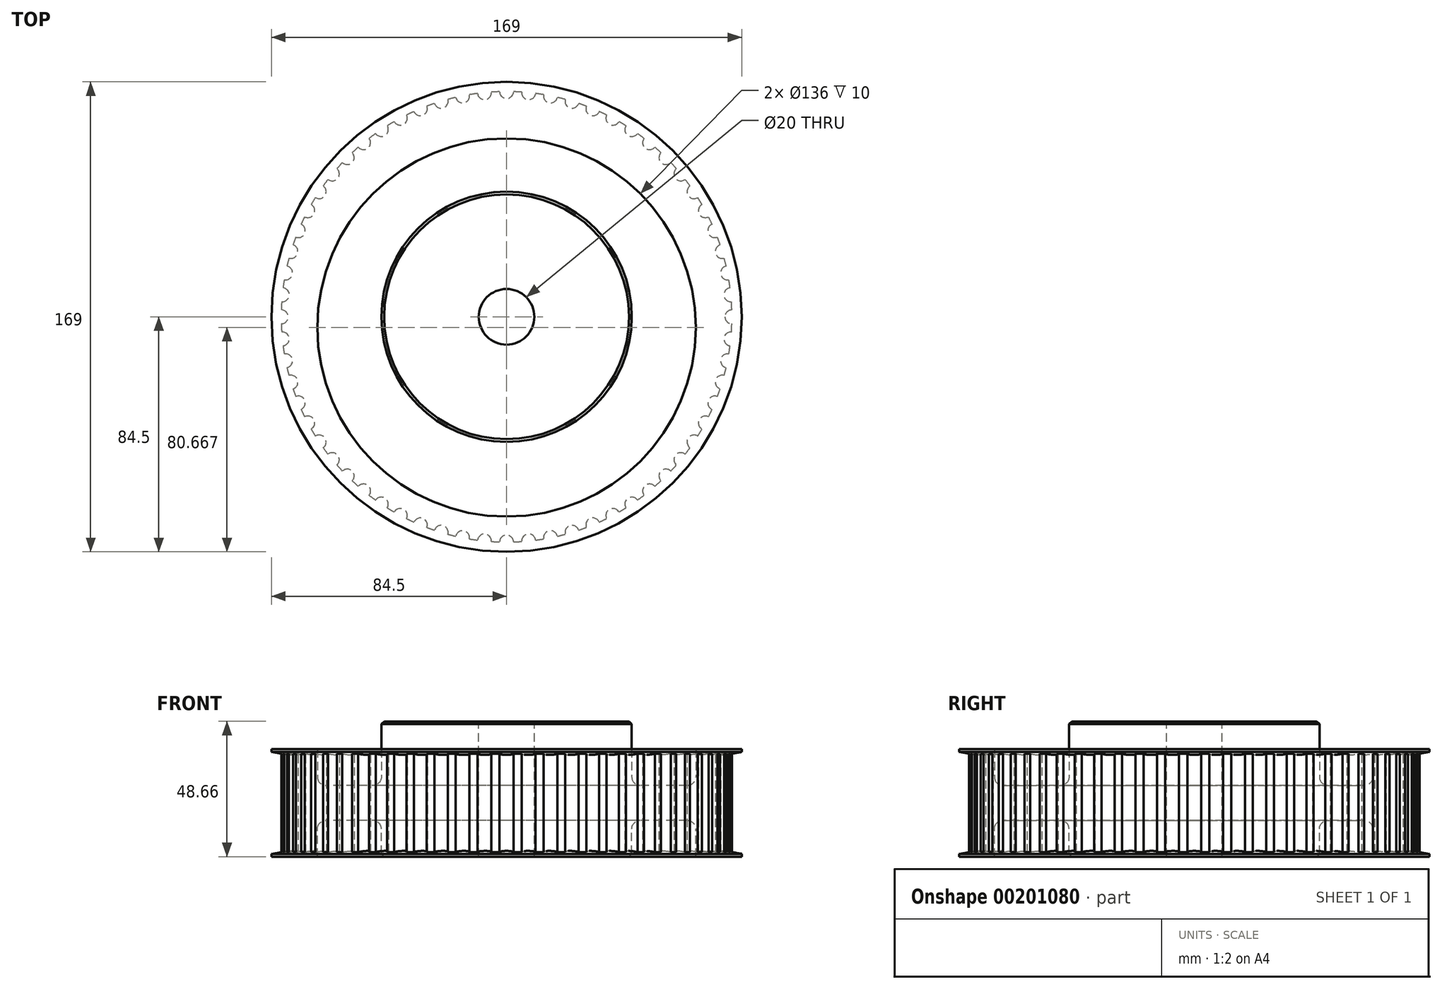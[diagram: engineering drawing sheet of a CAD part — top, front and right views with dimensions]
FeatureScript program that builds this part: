
annotation { "Feature Type Name" : "Feature", "Feature Type Description" : "" }
export const myFeature = defineFeature(function(context is Context, id is Id, definition is map)
    precondition{}
    {
        {
            var Q0;
            Q0=qCreatedBy(makeId("Top.planeOp"),FACE);
            var sketch = newSketch(context, id + "F0", { "sketchPlane" : qUnion([Q0])});
            skCircle(sketch, "E0", {"center": v(0, 0) * mm, "radius": 81 * mm});
            skCircle(sketch, "E1", {"center": v(0, 81) * mm, "radius": 2.5 * mm});
            skCircle(sketch, "E2.1.0", {"center": v(-7.94, 80.6) * mm, "radius": 2.5 * mm});
            skCircle(sketch, "E2.2.0", {"center": v(-15.8, 79.44) * mm, "radius": 2.5 * mm});
            skCircle(sketch, "E3.1.3.0", {"center": v(-23.51, 77.51) * mm, "radius": 2.5 * mm});
            skCircle(sketch, "E3.1.4.0", {"center": v(-31, 74.83) * mm, "radius": 2.5 * mm});
            skCircle(sketch, "E3.1.5.0", {"center": v(-38.18, 71.44) * mm, "radius": 2.5 * mm});
            skCircle(sketch, "E3.1.6.0", {"center": v(-45, 67.35) * mm, "radius": 2.5 * mm});
            skCircle(sketch, "E3.1.7.0", {"center": v(-51.39, 62.61) * mm, "radius": 2.5 * mm});
            skCircle(sketch, "E3.1.8.0", {"center": v(-57.28, 57.28) * mm, "radius": 2.5 * mm});
            skCircle(sketch, "E3.1.9.0", {"center": v(-62.61, 51.39) * mm, "radius": 2.5 * mm});
            skCircle(sketch, "E4.1.10.0", {"center": v(-67.35, 45) * mm, "radius": 2.5 * mm});
            skCircle(sketch, "E4.1.11.0", {"center": v(-71.44, 38.18) * mm, "radius": 2.5 * mm});
            skCircle(sketch, "E4.1.12.0", {"center": v(-74.83, 31) * mm, "radius": 2.5 * mm});
            skCircle(sketch, "E4.1.13.0", {"center": v(-77.51, 23.51) * mm, "radius": 2.5 * mm});
            skCircle(sketch, "E4.1.14.0", {"center": v(-79.44, 15.8) * mm, "radius": 2.5 * mm});
            skCircle(sketch, "E4.1.15.0", {"center": v(-80.6, 7.94) * mm, "radius": 2.5 * mm});
            skCircle(sketch, "E4.1.16.0", {"center": v(-81, 0) * mm, "radius": 2.5 * mm});
            skCircle(sketch, "E4.1.17.0", {"center": v(-80.6, -7.94) * mm, "radius": 2.5 * mm});
            skCircle(sketch, "E4.1.18.0", {"center": v(-79.44, -15.8) * mm, "radius": 2.5 * mm});
            skCircle(sketch, "E4.1.19.0", {"center": v(-77.51, -23.51) * mm, "radius": 2.5 * mm});
            skCircle(sketch, "E4.1.20.0", {"center": v(-74.83, -31) * mm, "radius": 2.5 * mm});
            skCircle(sketch, "E4.1.21.0", {"center": v(-71.44, -38.18) * mm, "radius": 2.5 * mm});
            skCircle(sketch, "E4.1.22.0", {"center": v(-67.35, -45) * mm, "radius": 2.5 * mm});
            skCircle(sketch, "E4.1.23.0", {"center": v(-62.61, -51.39) * mm, "radius": 2.5 * mm});
            skCircle(sketch, "E4.1.24.0", {"center": v(-57.28, -57.28) * mm, "radius": 2.5 * mm});
            skCircle(sketch, "E4.1.25.0", {"center": v(-51.39, -62.61) * mm, "radius": 2.5 * mm});
            skCircle(sketch, "E4.1.26.0", {"center": v(-45, -67.35) * mm, "radius": 2.5 * mm});
            skCircle(sketch, "E4.1.27.0", {"center": v(-38.18, -71.44) * mm, "radius": 2.5 * mm});
            skCircle(sketch, "E4.1.28.0", {"center": v(-31, -74.83) * mm, "radius": 2.5 * mm});
            skCircle(sketch, "E4.1.29.0", {"center": v(-23.51, -77.51) * mm, "radius": 2.5 * mm});
            skCircle(sketch, "E4.1.30.0", {"center": v(-15.8, -79.44) * mm, "radius": 2.5 * mm});
            skCircle(sketch, "E4.1.31.0", {"center": v(-7.94, -80.6) * mm, "radius": 2.5 * mm});
            skCircle(sketch, "E4.1.32.0", {"center": v(0, -81) * mm, "radius": 2.5 * mm});
            skCircle(sketch, "E4.1.33.0", {"center": v(7.94, -80.6) * mm, "radius": 2.5 * mm});
            skCircle(sketch, "E4.1.34.0", {"center": v(15.8, -79.44) * mm, "radius": 2.5 * mm});
            skCircle(sketch, "E4.1.35.0", {"center": v(23.51, -77.51) * mm, "radius": 2.5 * mm});
            skCircle(sketch, "E4.1.36.0", {"center": v(31, -74.83) * mm, "radius": 2.5 * mm});
            skCircle(sketch, "E4.1.37.0", {"center": v(38.18, -71.44) * mm, "radius": 2.5 * mm});
            skCircle(sketch, "E4.1.38.0", {"center": v(45, -67.35) * mm, "radius": 2.5 * mm});
            skCircle(sketch, "E4.1.39.0", {"center": v(51.39, -62.61) * mm, "radius": 2.5 * mm});
            skCircle(sketch, "E4.1.40.0", {"center": v(57.28, -57.28) * mm, "radius": 2.5 * mm});
            skCircle(sketch, "E4.1.41.0", {"center": v(62.61, -51.39) * mm, "radius": 2.5 * mm});
            skCircle(sketch, "E4.1.42.0", {"center": v(67.35, -45) * mm, "radius": 2.5 * mm});
            skCircle(sketch, "E4.1.43.0", {"center": v(71.44, -38.18) * mm, "radius": 2.5 * mm});
            skCircle(sketch, "E4.1.44.0", {"center": v(74.83, -31) * mm, "radius": 2.5 * mm});
            skCircle(sketch, "E4.1.45.0", {"center": v(77.51, -23.51) * mm, "radius": 2.5 * mm});
            skCircle(sketch, "E4.1.46.0", {"center": v(79.44, -15.8) * mm, "radius": 2.5 * mm});
            skCircle(sketch, "E4.1.47.0", {"center": v(80.6, -7.94) * mm, "radius": 2.5 * mm});
            skCircle(sketch, "E4.1.48.0", {"center": v(81, 0) * mm, "radius": 2.5 * mm});
            skCircle(sketch, "E4.1.49.0", {"center": v(80.6, 7.94) * mm, "radius": 2.5 * mm});
            skCircle(sketch, "E4.1.50.0", {"center": v(79.44, 15.8) * mm, "radius": 2.5 * mm});
            skCircle(sketch, "E4.1.51.0", {"center": v(77.51, 23.51) * mm, "radius": 2.5 * mm});
            skCircle(sketch, "E4.1.52.0", {"center": v(74.83, 31) * mm, "radius": 2.5 * mm});
            skCircle(sketch, "E4.1.53.0", {"center": v(71.44, 38.18) * mm, "radius": 2.5 * mm});
            skCircle(sketch, "E4.1.54.0", {"center": v(67.35, 45) * mm, "radius": 2.5 * mm});
            skCircle(sketch, "E4.1.55.0", {"center": v(62.61, 51.39) * mm, "radius": 2.5 * mm});
            skCircle(sketch, "E4.1.56.0", {"center": v(57.28, 57.28) * mm, "radius": 2.5 * mm});
            skCircle(sketch, "E4.1.57.0", {"center": v(51.39, 62.61) * mm, "radius": 2.5 * mm});
            skCircle(sketch, "E4.1.58.0", {"center": v(45, 67.35) * mm, "radius": 2.5 * mm});
            skCircle(sketch, "E4.1.59.0", {"center": v(38.18, 71.44) * mm, "radius": 2.5 * mm});
            skCircle(sketch, "E4.1.60.0", {"center": v(31, 74.83) * mm, "radius": 2.5 * mm});
            skCircle(sketch, "E4.1.61.0", {"center": v(23.51, 77.51) * mm, "radius": 2.5 * mm});
            skCircle(sketch, "E4.1.62.0", {"center": v(15.8, 79.44) * mm, "radius": 2.5 * mm});
            skCircle(sketch, "E4.1.63.0", {"center": v(7.94, 80.6) * mm, "radius": 2.5 * mm});
            skSolve(sketch);
        }
        {
            var Q0;
            Q0=makeQuery(id+"F0.imprint","IMPRINT",FACE,{"disambiguationData":[TD([[makeQuery(id+"F0.imprint","IMPRINT",EDGE,{"derivedFrom":sQuery(id+"F0.wireOp",EDGE,"E0")}),1.0]])]});
            extrude(context, id + "F1", {"entities" : qUnion([Q0]), "depth" : (32.65 / 2) * mm});
        }
        {
            var Q0;
            Q0=makeQuery(id+"F1.opExtrude","CAP_FACE",FACE,{"disambiguationData":[OSD([sQuery(id+"F0.wireOp",EDGE,"E0"),sQuery(id+"F0.wireOp",EDGE,"E1"),sQuery(id+"F0.wireOp",EDGE,"E2.1.0"),sQuery(id+"F0.wireOp",EDGE,"E2.2.0"),sQuery(id+"F0.wireOp",EDGE,"E3.1.3.0"),sQuery(id+"F0.wireOp",EDGE,"E3.1.4.0"),sQuery(id+"F0.wireOp",EDGE,"E3.1.5.0"),sQuery(id+"F0.wireOp",EDGE,"E3.1.6.0"),sQuery(id+"F0.wireOp",EDGE,"E3.1.7.0"),sQuery(id+"F0.wireOp",EDGE,"E3.1.8.0"),sQuery(id+"F0.wireOp",EDGE,"E3.1.9.0"),sQuery(id+"F0.wireOp",EDGE,"E4.1.10.0"),sQuery(id+"F0.wireOp",EDGE,"E4.1.11.0"),sQuery(id+"F0.wireOp",EDGE,"E4.1.12.0"),sQuery(id+"F0.wireOp",EDGE,"E4.1.13.0"),sQuery(id+"F0.wireOp",EDGE,"E4.1.14.0"),sQuery(id+"F0.wireOp",EDGE,"E4.1.15.0"),sQuery(id+"F0.wireOp",EDGE,"E4.1.16.0"),sQuery(id+"F0.wireOp",EDGE,"E4.1.17.0"),sQuery(id+"F0.wireOp",EDGE,"E4.1.18.0"),sQuery(id+"F0.wireOp",EDGE,"E4.1.19.0"),sQuery(id+"F0.wireOp",EDGE,"E4.1.20.0"),sQuery(id+"F0.wireOp",EDGE,"E4.1.21.0"),sQuery(id+"F0.wireOp",EDGE,"E4.1.22.0"),sQuery(id+"F0.wireOp",EDGE,"E4.1.23.0"),sQuery(id+"F0.wireOp",EDGE,"E4.1.24.0"),sQuery(id+"F0.wireOp",EDGE,"E4.1.25.0"),sQuery(id+"F0.wireOp",EDGE,"E4.1.26.0"),sQuery(id+"F0.wireOp",EDGE,"E4.1.27.0"),sQuery(id+"F0.wireOp",EDGE,"E4.1.28.0"),sQuery(id+"F0.wireOp",EDGE,"E4.1.29.0"),sQuery(id+"F0.wireOp",EDGE,"E4.1.30.0"),sQuery(id+"F0.wireOp",EDGE,"E4.1.31.0"),sQuery(id+"F0.wireOp",EDGE,"E4.1.32.0"),sQuery(id+"F0.wireOp",EDGE,"E4.1.33.0"),sQuery(id+"F0.wireOp",EDGE,"E4.1.34.0"),sQuery(id+"F0.wireOp",EDGE,"E4.1.35.0"),sQuery(id+"F0.wireOp",EDGE,"E4.1.36.0"),sQuery(id+"F0.wireOp",EDGE,"E4.1.37.0"),sQuery(id+"F0.wireOp",EDGE,"E4.1.38.0"),sQuery(id+"F0.wireOp",EDGE,"E4.1.39.0"),sQuery(id+"F0.wireOp",EDGE,"E4.1.40.0"),sQuery(id+"F0.wireOp",EDGE,"E4.1.41.0"),sQuery(id+"F0.wireOp",EDGE,"E4.1.42.0"),sQuery(id+"F0.wireOp",EDGE,"E4.1.43.0"),sQuery(id+"F0.wireOp",EDGE,"E4.1.44.0"),sQuery(id+"F0.wireOp",EDGE,"E4.1.45.0"),sQuery(id+"F0.wireOp",EDGE,"E4.1.46.0"),sQuery(id+"F0.wireOp",EDGE,"E4.1.47.0"),sQuery(id+"F0.wireOp",EDGE,"E4.1.48.0"),sQuery(id+"F0.wireOp",EDGE,"E4.1.49.0"),sQuery(id+"F0.wireOp",EDGE,"E4.1.50.0"),sQuery(id+"F0.wireOp",EDGE,"E4.1.51.0"),sQuery(id+"F0.wireOp",EDGE,"E4.1.52.0"),sQuery(id+"F0.wireOp",EDGE,"E4.1.53.0"),sQuery(id+"F0.wireOp",EDGE,"E4.1.54.0"),sQuery(id+"F0.wireOp",EDGE,"E4.1.55.0"),sQuery(id+"F0.wireOp",EDGE,"E4.1.56.0"),sQuery(id+"F0.wireOp",EDGE,"E4.1.57.0"),sQuery(id+"F0.wireOp",EDGE,"E4.1.58.0"),sQuery(id+"F0.wireOp",EDGE,"E4.1.59.0"),sQuery(id+"F0.wireOp",EDGE,"E4.1.60.0"),sQuery(id+"F0.wireOp",EDGE,"E4.1.61.0"),sQuery(id+"F0.wireOp",EDGE,"E4.1.62.0"),sQuery(id+"F0.wireOp",EDGE,"E4.1.63.0")])],"isStart":false});
            var sketch = newSketch(context, id + "F2", { "sketchPlane" : qUnion([Q0])});
            skCircle(sketch, "E5", {"center": v(0, 0) * mm, "radius": 45 * mm});
            skCircle(sketch, "E6", {"center": v(0, 0) * mm, "radius": 84.5 * mm});
            skCircle(sketch, "E7", {"center": v(0, -3.83) * mm, "radius": 68 * mm});
            skSolve(sketch);
        }
        {
            var Q0;
            Q0=makeQuery(id+"F2.imprint","IMPRINT",FACE,{"disambiguationData":[TD([[makeQuery(id+"F2.imprint","IMPRINT",EDGE,{"derivedFrom":sQuery(id+"F2.wireOp",EDGE,"E6")}),1.0]])]});
            var Q1;
            Q1=makeQuery(id+"F2.imprint","IMPRINT",FACE,{"disambiguationData":[TD([[makeQuery(id+"F2.imprint","IMPRINT",EDGE,{"derivedFrom":sQuery(id+"F2.wireOp",EDGE,"E7")}),-1.0]])]});
            extrude(context, id + "F3", {"entities" : qUnion([Q0, Q1]), "operationType" : NewBodyOperationType.ADD, "depth" : 3 * mm});
        }
        {
            var Q0;
            Q0=makeQuery(id+"F2.imprint","IMPRINT",FACE,{"disambiguationData":[TD([[makeQuery(id+"F2.imprint","IMPRINT",EDGE,{"derivedFrom":sQuery(id+"F2.wireOp",EDGE,"E5")}),1.0]])]});
            extrude(context, id + "F4", {"entities" : qUnion([Q0]), "operationType" : NewBodyOperationType.ADD, "depth" : 3 * mm});
        }
        {
            var Q0;
            Q0=makeQuery(id+"F2.imprint","IMPRINT",FACE,{"disambiguationData":[TD([[makeQuery(id+"F2.imprint","IMPRINT",EDGE,{"derivedFrom":sQuery(id+"F2.wireOp",EDGE,"E5")}),-1.0]])]});
            extrude(context, id + "F5", {"entities" : qUnion([Q0]), "operationType" : NewBodyOperationType.REMOVE, "oppositeDirection" : true, "depth" : 10 * mm});
        }
        {
            var Q0;
            Q0=makeQuery(id+"F3.opExtrude","CAP_EDGE",EDGE,{"disambiguationData":[OSD([sQuery(id+"F2.wireOp",EDGE,"E6")])],"isStart":true});
            chamfer(context, id + "F6", {"entities" : qUnion([Q0]), "chamferType" : ChamferType.OFFSET_ANGLE, "width" : 2 * mm, "oppositeDirection" : false, "angle" : 80 * degree, "tangentPropagation" : true});
        }
        {
            var Q0;
            Q0=makeQuery(id+"F5.boolean.opBoolean","COPY",FACE,{"derivedFrom":makeQuery(id+"F5.opExtrude","CAP_FACE",FACE,{"disambiguationData":[OSD([sQuery(id+"F2.wireOp",EDGE,"E5"),sQuery(id+"F2.wireOp",EDGE,"E7")])],"isStart":false})});
            fillet(context, id + "F7", {"entities" : qUnion([Q0]), "radius" : 3 * mm, "tangentPropagation" : true, "allowEdgeOverflow" : false});
        }
        {
            var Q0;
            Q0=makeQuery(id+"F1.opExtrude","SWEPT_BODY",BODY,{"disambiguationData":[OSD([sQuery(id+"F0.wireOp",EDGE,"E0"),sQuery(id+"F0.wireOp",EDGE,"E1"),sQuery(id+"F0.wireOp",EDGE,"E2.1.0"),sQuery(id+"F0.wireOp",EDGE,"E2.2.0"),sQuery(id+"F0.wireOp",EDGE,"E3.1.3.0"),sQuery(id+"F0.wireOp",EDGE,"E3.1.4.0"),sQuery(id+"F0.wireOp",EDGE,"E3.1.5.0"),sQuery(id+"F0.wireOp",EDGE,"E3.1.6.0"),sQuery(id+"F0.wireOp",EDGE,"E3.1.7.0"),sQuery(id+"F0.wireOp",EDGE,"E3.1.8.0"),sQuery(id+"F0.wireOp",EDGE,"E3.1.9.0"),sQuery(id+"F0.wireOp",EDGE,"E4.1.10.0"),sQuery(id+"F0.wireOp",EDGE,"E4.1.11.0"),sQuery(id+"F0.wireOp",EDGE,"E4.1.12.0"),sQuery(id+"F0.wireOp",EDGE,"E4.1.13.0"),sQuery(id+"F0.wireOp",EDGE,"E4.1.14.0"),sQuery(id+"F0.wireOp",EDGE,"E4.1.15.0"),sQuery(id+"F0.wireOp",EDGE,"E4.1.16.0"),sQuery(id+"F0.wireOp",EDGE,"E4.1.17.0"),sQuery(id+"F0.wireOp",EDGE,"E4.1.18.0"),sQuery(id+"F0.wireOp",EDGE,"E4.1.19.0"),sQuery(id+"F0.wireOp",EDGE,"E4.1.20.0"),sQuery(id+"F0.wireOp",EDGE,"E4.1.21.0"),sQuery(id+"F0.wireOp",EDGE,"E4.1.22.0"),sQuery(id+"F0.wireOp",EDGE,"E4.1.23.0"),sQuery(id+"F0.wireOp",EDGE,"E4.1.24.0"),sQuery(id+"F0.wireOp",EDGE,"E4.1.25.0"),sQuery(id+"F0.wireOp",EDGE,"E4.1.26.0"),sQuery(id+"F0.wireOp",EDGE,"E4.1.27.0"),sQuery(id+"F0.wireOp",EDGE,"E4.1.28.0"),sQuery(id+"F0.wireOp",EDGE,"E4.1.29.0"),sQuery(id+"F0.wireOp",EDGE,"E4.1.30.0"),sQuery(id+"F0.wireOp",EDGE,"E4.1.31.0"),sQuery(id+"F0.wireOp",EDGE,"E4.1.32.0"),sQuery(id+"F0.wireOp",EDGE,"E4.1.33.0"),sQuery(id+"F0.wireOp",EDGE,"E4.1.34.0"),sQuery(id+"F0.wireOp",EDGE,"E4.1.35.0"),sQuery(id+"F0.wireOp",EDGE,"E4.1.36.0"),sQuery(id+"F0.wireOp",EDGE,"E4.1.37.0"),sQuery(id+"F0.wireOp",EDGE,"E4.1.38.0"),sQuery(id+"F0.wireOp",EDGE,"E4.1.39.0"),sQuery(id+"F0.wireOp",EDGE,"E4.1.40.0"),sQuery(id+"F0.wireOp",EDGE,"E4.1.41.0"),sQuery(id+"F0.wireOp",EDGE,"E4.1.42.0"),sQuery(id+"F0.wireOp",EDGE,"E4.1.43.0"),sQuery(id+"F0.wireOp",EDGE,"E4.1.44.0"),sQuery(id+"F0.wireOp",EDGE,"E4.1.45.0"),sQuery(id+"F0.wireOp",EDGE,"E4.1.46.0"),sQuery(id+"F0.wireOp",EDGE,"E4.1.47.0"),sQuery(id+"F0.wireOp",EDGE,"E4.1.48.0"),sQuery(id+"F0.wireOp",EDGE,"E4.1.49.0"),sQuery(id+"F0.wireOp",EDGE,"E4.1.50.0"),sQuery(id+"F0.wireOp",EDGE,"E4.1.51.0"),sQuery(id+"F0.wireOp",EDGE,"E4.1.52.0"),sQuery(id+"F0.wireOp",EDGE,"E4.1.53.0"),sQuery(id+"F0.wireOp",EDGE,"E4.1.54.0"),sQuery(id+"F0.wireOp",EDGE,"E4.1.55.0"),sQuery(id+"F0.wireOp",EDGE,"E4.1.56.0"),sQuery(id+"F0.wireOp",EDGE,"E4.1.57.0"),sQuery(id+"F0.wireOp",EDGE,"E4.1.58.0"),sQuery(id+"F0.wireOp",EDGE,"E4.1.59.0"),sQuery(id+"F0.wireOp",EDGE,"E4.1.60.0"),sQuery(id+"F0.wireOp",EDGE,"E4.1.61.0"),sQuery(id+"F0.wireOp",EDGE,"E4.1.62.0"),sQuery(id+"F0.wireOp",EDGE,"E4.1.63.0")])]});
            var Q1;
            Q1=qCreatedBy(makeId("Top.planeOp"),FACE);
            mirror(context, id + "F8", {"operationType" : NewBodyOperationType.ADD, "entities" : qUnion([Q0]), "mirrorPlane" : qUnion([Q1])});
        }
        {
            var Q0;
            Q0=makeQuery(id+"F4.opExtrude","CAP_FACE",FACE,{"disambiguationData":[OSD([sQuery(id+"F2.wireOp",EDGE,"E5")])],"isStart":false});
            extrude(context, id + "F9", {"entities" : qUnion([Q0]), "operationType" : NewBodyOperationType.ADD, "depth" : 10 * mm});
        }
        {
            var Q0;
            Q0=makeQuery(id+"F9.opExtrude","CAP_EDGE",EDGE,{"disambiguationData":[OSD([sQuery(id+"F2.wireOp",EDGE,"E5")])],"isStart":false});
            var Q1;
            Q1=makeQuery(id+"F8.opPattern","COPY",EDGE,{"derivedFrom":makeQuery(id+"F4.opExtrude","CAP_EDGE",EDGE,{"disambiguationData":[OSD([sQuery(id+"F2.wireOp",EDGE,"E5")])],"isStart":false}),"instanceName":"1"});
            chamfer(context, id + "F10", {"entities" : qUnion([Q0, Q1]), "width" : 1 * mm, "tangentPropagation" : true});
        }
        {
            var Q0;
            Q0=makeQuery(id+"F9.opExtrude","CAP_FACE",FACE,{"disambiguationData":[OSD([sQuery(id+"F2.wireOp",EDGE,"E5")])],"isStart":false});
            var sketch = newSketch(context, id + "F11", { "sketchPlane" : qUnion([Q0])});
            skPoint(sketch, "E8", {"position": v(0, 0) * mm});
            skSolve(sketch);
        }
        {
            var Q0;
            Q0=sQuery(id+"F11.wireOp",VERTEX,"E8");
            var Q1;
            Q1=makeQuery(id+"F1.opExtrude","SWEPT_BODY",BODY,{"disambiguationData":[OSD([sQuery(id+"F0.wireOp",EDGE,"E0"),sQuery(id+"F0.wireOp",EDGE,"E1"),sQuery(id+"F0.wireOp",EDGE,"E2.1.0"),sQuery(id+"F0.wireOp",EDGE,"E2.2.0"),sQuery(id+"F0.wireOp",EDGE,"E3.1.3.0"),sQuery(id+"F0.wireOp",EDGE,"E3.1.4.0"),sQuery(id+"F0.wireOp",EDGE,"E3.1.5.0"),sQuery(id+"F0.wireOp",EDGE,"E3.1.6.0"),sQuery(id+"F0.wireOp",EDGE,"E3.1.7.0"),sQuery(id+"F0.wireOp",EDGE,"E3.1.8.0"),sQuery(id+"F0.wireOp",EDGE,"E3.1.9.0"),sQuery(id+"F0.wireOp",EDGE,"E4.1.10.0"),sQuery(id+"F0.wireOp",EDGE,"E4.1.11.0"),sQuery(id+"F0.wireOp",EDGE,"E4.1.12.0"),sQuery(id+"F0.wireOp",EDGE,"E4.1.13.0"),sQuery(id+"F0.wireOp",EDGE,"E4.1.14.0"),sQuery(id+"F0.wireOp",EDGE,"E4.1.15.0"),sQuery(id+"F0.wireOp",EDGE,"E4.1.16.0"),sQuery(id+"F0.wireOp",EDGE,"E4.1.17.0"),sQuery(id+"F0.wireOp",EDGE,"E4.1.18.0"),sQuery(id+"F0.wireOp",EDGE,"E4.1.19.0"),sQuery(id+"F0.wireOp",EDGE,"E4.1.20.0"),sQuery(id+"F0.wireOp",EDGE,"E4.1.21.0"),sQuery(id+"F0.wireOp",EDGE,"E4.1.22.0"),sQuery(id+"F0.wireOp",EDGE,"E4.1.23.0"),sQuery(id+"F0.wireOp",EDGE,"E4.1.24.0"),sQuery(id+"F0.wireOp",EDGE,"E4.1.25.0"),sQuery(id+"F0.wireOp",EDGE,"E4.1.26.0"),sQuery(id+"F0.wireOp",EDGE,"E4.1.27.0"),sQuery(id+"F0.wireOp",EDGE,"E4.1.28.0"),sQuery(id+"F0.wireOp",EDGE,"E4.1.29.0"),sQuery(id+"F0.wireOp",EDGE,"E4.1.30.0"),sQuery(id+"F0.wireOp",EDGE,"E4.1.31.0"),sQuery(id+"F0.wireOp",EDGE,"E4.1.32.0"),sQuery(id+"F0.wireOp",EDGE,"E4.1.33.0"),sQuery(id+"F0.wireOp",EDGE,"E4.1.34.0"),sQuery(id+"F0.wireOp",EDGE,"E4.1.35.0"),sQuery(id+"F0.wireOp",EDGE,"E4.1.36.0"),sQuery(id+"F0.wireOp",EDGE,"E4.1.37.0"),sQuery(id+"F0.wireOp",EDGE,"E4.1.38.0"),sQuery(id+"F0.wireOp",EDGE,"E4.1.39.0"),sQuery(id+"F0.wireOp",EDGE,"E4.1.40.0"),sQuery(id+"F0.wireOp",EDGE,"E4.1.41.0"),sQuery(id+"F0.wireOp",EDGE,"E4.1.42.0"),sQuery(id+"F0.wireOp",EDGE,"E4.1.43.0"),sQuery(id+"F0.wireOp",EDGE,"E4.1.44.0"),sQuery(id+"F0.wireOp",EDGE,"E4.1.45.0"),sQuery(id+"F0.wireOp",EDGE,"E4.1.46.0"),sQuery(id+"F0.wireOp",EDGE,"E4.1.47.0"),sQuery(id+"F0.wireOp",EDGE,"E4.1.48.0"),sQuery(id+"F0.wireOp",EDGE,"E4.1.49.0"),sQuery(id+"F0.wireOp",EDGE,"E4.1.50.0"),sQuery(id+"F0.wireOp",EDGE,"E4.1.51.0"),sQuery(id+"F0.wireOp",EDGE,"E4.1.52.0"),sQuery(id+"F0.wireOp",EDGE,"E4.1.53.0"),sQuery(id+"F0.wireOp",EDGE,"E4.1.54.0"),sQuery(id+"F0.wireOp",EDGE,"E4.1.55.0"),sQuery(id+"F0.wireOp",EDGE,"E4.1.56.0"),sQuery(id+"F0.wireOp",EDGE,"E4.1.57.0"),sQuery(id+"F0.wireOp",EDGE,"E4.1.58.0"),sQuery(id+"F0.wireOp",EDGE,"E4.1.59.0"),sQuery(id+"F0.wireOp",EDGE,"E4.1.60.0"),sQuery(id+"F0.wireOp",EDGE,"E4.1.61.0"),sQuery(id+"F0.wireOp",EDGE,"E4.1.62.0"),sQuery(id+"F0.wireOp",EDGE,"E4.1.63.0")])]});
            hole(context, id + "F12", {"style" : HoleStyle.SIMPLE, "endStyle" : HoleEndStyle.THROUGH, "holeDiameter" : 20 * mm, "startFromSketch" : true, "locations" : qUnion([Q0]), "scope" : qUnion([Q1]), "isTappedThrough" : true});
        }
    });
